# Revit family: RISE1x4
name_source: partatom
category: Lighting Fixtures
units: mm (PartAtom-declared; Revit-internal decimal feet)

## family parameters
Always vertical = Yes
Cut with Voids When Loaded = No
Host = Ceiling
Light Source = Yes
Maintain Annotation Orientation = No
OmniClass Number = 23.80.70.11.14.17
OmniClass Title = Direct/Indirect
Part Type = Normal
Room Calculation Point = No
Round Connector Dimension = Use Diameter
Shared = No

## types (4) — shared parameters
Assembly Code = D5020200
Color Filter = 16777215
Default Elevation = 0' - 0"
Description = LED  Architectural Recessed Troffer Luminaire
Dimming Lamp Color Temperature Shift = <None>
Emit Shape Visible in Rendering = No
Emit from Rectangle Length = 3' - 11 3/4"
Emit from Rectangle Width = 0' - 11 3/4"
Height = 0' - 2"
Housing Finish = Metal - Viscor - White
Lamp = LED
Length = 3' - 11 3/4"
Lens Finish = Polycarbonate - Viscor - Frosted Round
Manufacturer = VISIONEERING by VISCOR
Model = RISE
Tile Finish = Panel Tile
Tilt Angle = 90.00°
URL = https://viscor.com
Voltage = 120 V
Width = 0' - 11 3/4"

## per-type parameters (varying)
| type | Apparent Load | Lamp Wattage | Photometric Web File |
| RISE1X4-LED840K052LUNV | 40 VA | 40 VA | RISE1X4-LED840K052LUNV.ies |
| RISE1X4-LED840K027LUNV | 20 VA | 20 VA | RISE1X4-LED840K027LUNV.ies |
| RISE1X4-LED840K064LUNV | 50 VA | 50 VA | RISE1X4-LED840K064LUNV.ies |
| RISE1X4-LED840K039LUNV | 30 VA | 30 VA | RISE1X4-LED840K039LUNV.ies |

## geometry (parser evidence)
native form markers: Sweep x3
no freeform markers — native parametric forms only
